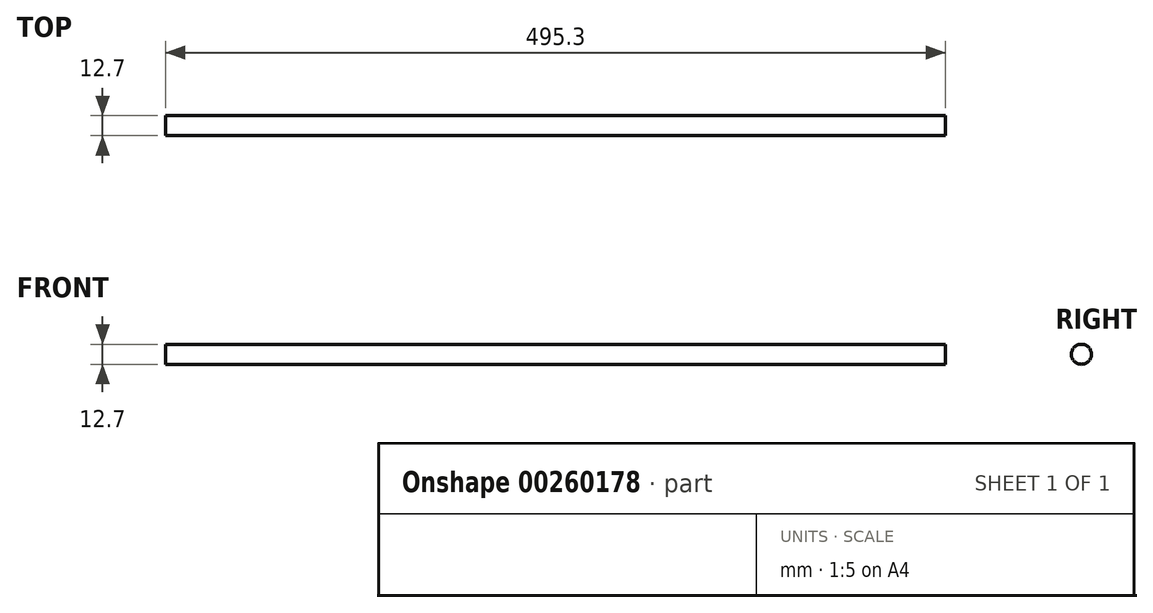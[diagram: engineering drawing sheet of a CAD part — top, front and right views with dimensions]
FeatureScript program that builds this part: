
annotation { "Feature Type Name" : "Feature", "Feature Type Description" : "" }
export const myFeature = defineFeature(function(context is Context, id is Id, definition is map)
    precondition{}
    {
        {
            var Q0;
            Q0=qCreatedBy(makeId("Right.planeOp"),FACE);
            var sketch = newSketch(context, id + "F0", { "sketchPlane" : qUnion([Q0])});
            skCircle(sketch, "E0", {"center": v(12.41, -6.92) * mm, "radius": 6.35 * mm});
            skSolve(sketch);
        }
        {
            var Q0;
            Q0 = qSketchRegion(id + "F0", true);
            extrude(context, id + "F1", {"entities" : qUnion([Q0]), "depth" : 495.3 * mm});
        }
    });
